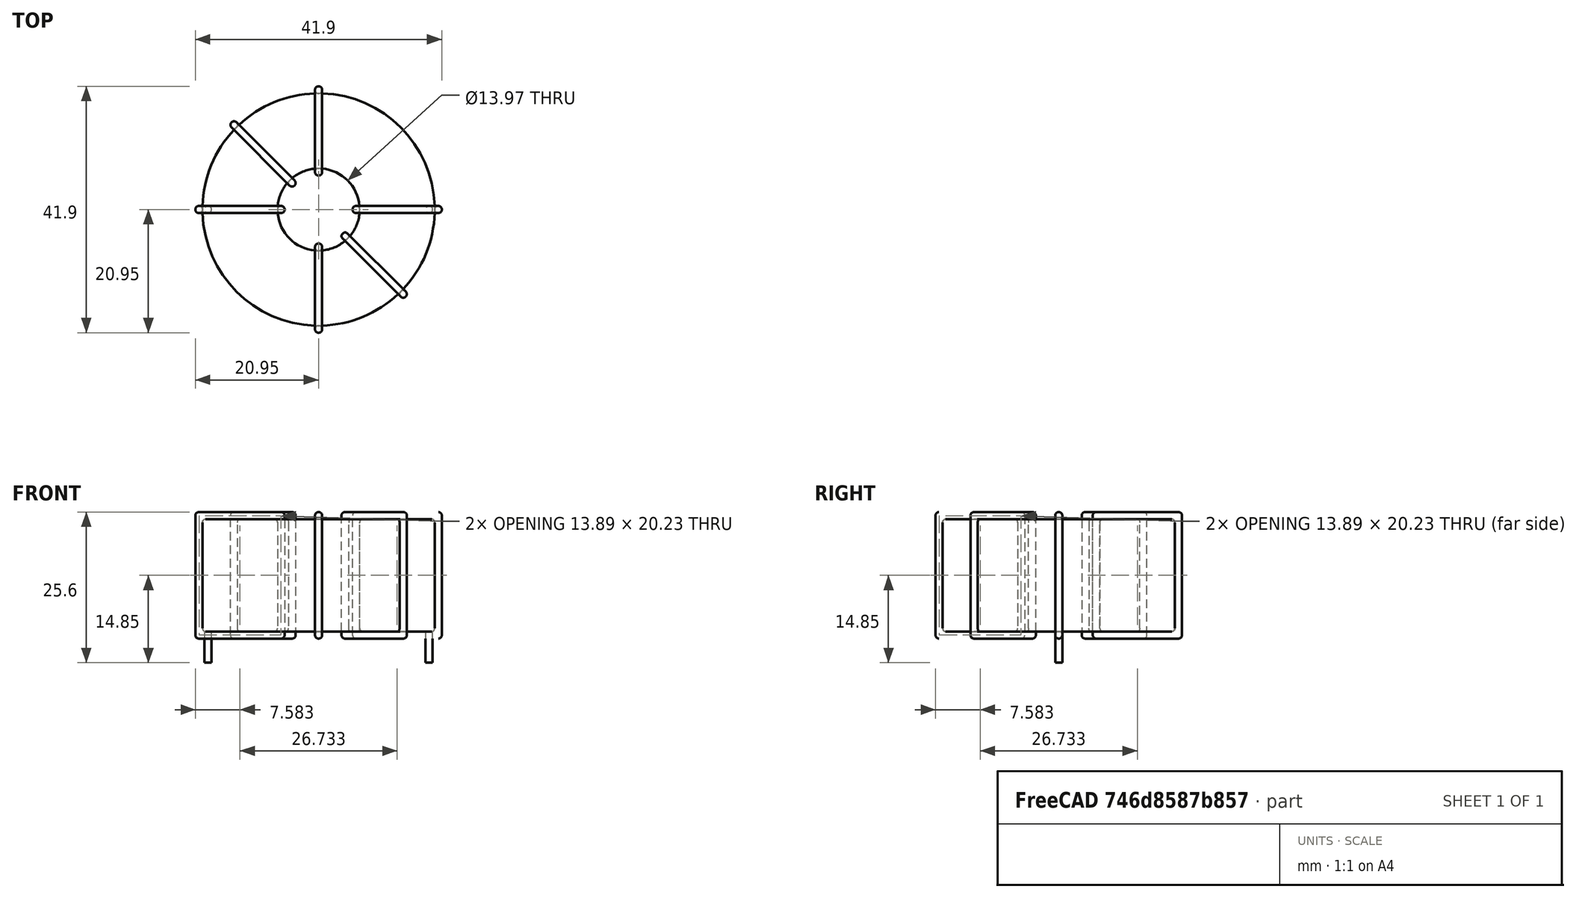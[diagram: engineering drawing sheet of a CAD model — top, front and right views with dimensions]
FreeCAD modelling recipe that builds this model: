
FCSTD DOCUMENT  (FreeCAD 0.16R6703 (Git))
Label: L_Toroid_Horizontal_D41.9mm_P37.60mm_Vishay_TJ7
License: All rights reserved
LicenseURL: http://en.wikipedia.org/wiki/All_rights_reserved
objects: Sketcher::SketchObject×6, PartDesign::Pad×6, PartDesign::Fillet×5, Spreadsheet::Sheet×1
note: 23 computed .brp shape members not serialized (recipe doc carries the construction recipe); baked Part::Feature solids carry a one-line shape summary decoded from their .brp

FEATURE [Spreadsheet::Sheet] Spreadsheet  label="dimensions"
  cells = A1=Wx; B1(Wx)=41.9; C1(WW)=13.96666666666667; D1=41.9; A2=Wy; B2(Wy)=41.9; D2=41.9; A3=RM; B3(RMx)=37.6; C3(RMy)=0; A4=d_wire; B4(d_wire)=1.2; A5=H; B5(H)=19.1; A6=offsetx; B6(offsetx)=2.149999999999999
FEATURE [Sketcher::SketchObject] Sketch
  Placement = pos=(0,0,1.7) rot=(0,0,1;0rad)
  expr: Placement.Base.z = 0.5 + Spreadsheet.d_wire
  expr: Constraints[0] = Spreadsheet.Wx / 2 - Spreadsheet.d_wire
  expr: Constraints[4] = Spreadsheet.WW / 2
  expr: Constraints[2] = Spreadsheet.RMy / 2
  expr: Constraints[1] = Spreadsheet.RMx / 2
  sketch-geometry (2):
    g0: Circle CenterX=18.8 CenterY=0 CenterZ=0 NormalX=0 NormalY=0 NormalZ=1 Radius=19.75
    g1: Circle CenterX=18.8 CenterY=0 CenterZ=0 NormalX=0 NormalY=0 NormalZ=1 Radius=6.98333
  constraints (5):
    c: Radius(g0) = 19.75
    c: DistanceX(g-1,g0) = 18.8
    c: DistanceY(g-1,g0) = 0
    c: Coincident(g1,g0)
    c: Radius(g1) = 6.98333
FEATURE [PartDesign::Pad] Pad
  Length = 19.1
  Length2 = 100
  Placement = pos=(0,0,1.7) rot=(0,0,1;0rad)
  Sketch = -> Sketch
  Type = 0
  expr: Length = Spreadsheet.H
FEATURE [Sketcher::SketchObject] Sketch001
  Placement = pos=(0,0,1.1) rot=(0,0,1;0rad)
  expr: Placement.Base.z = 0.5 + Spreadsheet.d_wire * 0.5
  expr: Constraints[4] = Spreadsheet.RMx
  expr: Constraints[2] = Spreadsheet.RMy
  expr: Constraints[1] = Spreadsheet.d_wire / 2
  sketch-geometry (2):
    g0: Circle CenterX=0 CenterY=0 CenterZ=0 NormalX=0 NormalY=0 NormalZ=1 Radius=0.6
    g1: Circle CenterX=37.6 CenterY=0 CenterZ=0 NormalX=0 NormalY=0 NormalZ=1 Radius=0.6
  constraints (5):
    c: Equal(g0,g1)
    c: Radius(g0) = 0.6
    c: DistanceY(g-1,g1) = 0
    c: Coincident(g0,g-1)
    c: DistanceX(g-1,g1) = 37.6
FEATURE [PartDesign::Pad] Pad001
  Length = 0.6
  Length2 = 4.7
  Placement = pos=(0,0,1.1) rot=(0,0,1;0rad)
  Reversed = true
  Sketch = -> Sketch001
  Type = 4
  expr: Length2 = 3.5 + Spreadsheet.d_wire
  expr: Length = Spreadsheet.d_wire / 2
FEATURE [PartDesign::Fillet] Fillet
  Base = -> Pad [Edge6,Edge3,Edge2]
  Placement = pos=(0,0,1.7) rot=(0,0,1;0rad)
  Radius = 0.5
FEATURE [Sketcher::SketchObject] Sketch003
  Placement = pos=(18.8,0,0) rot=(1,0,0;1.5708rad)
  expr: Placement.Base.x = Spreadsheet.RMx / 2
  expr: Constraints[49] = Spreadsheet.Wx - Spreadsheet.d_wire * 2
  expr: Constraints[44] = Spreadsheet.d_wire
  expr: Constraints[23] = Spreadsheet.H
  expr: Constraints[22] = Spreadsheet.Wx / 2 - Spreadsheet.d_wire
  expr: Placement.Base.y = Spreadsheet.RMy / 2
  expr: Constraints[21] = (Spreadsheet.Wx - Spreadsheet.WW) / 2 - Spreadsheet.d_wire
  expr: Constraints[19] = Spreadsheet.d_wire
  expr: Constraints[17] = Spreadsheet.d_wire
  expr: Constraints[18] = Spreadsheet.d_wire
  expr: Constraints[16] = Spreadsheet.d_wire
  sketch-geometry (16):
    g0: LineSegment StartX=-5.78333 StartY=0.5 StartZ=0 EndX=-20.95 EndY=0.5 EndZ=0
    g1: LineSegment StartX=-20.95 StartY=0.5 StartZ=0 EndX=-20.95 EndY=22 EndZ=0
    g2: LineSegment StartX=-20.95 StartY=22 StartZ=0 EndX=-5.78333 EndY=22 EndZ=0
    g3: LineSegment StartX=-5.78333 StartY=22 StartZ=0 EndX=-5.78333 EndY=0.5 EndZ=0
    g4: LineSegment StartX=-19.75 StartY=20.8 StartZ=0 EndX=-6.98333 EndY=20.8 EndZ=0
    g5: LineSegment StartX=-6.98333 StartY=20.8 StartZ=0 EndX=-6.98333 EndY=1.7 EndZ=0
    g6: LineSegment StartX=-6.98333 StartY=1.7 StartZ=0 EndX=-19.75 EndY=1.7 EndZ=0
    g7: LineSegment StartX=-19.75 StartY=1.7 StartZ=0 EndX=-19.75 EndY=20.8 EndZ=0
    g8: LineSegment StartX=5.78333 StartY=22 StartZ=0 EndX=20.95 EndY=22 EndZ=0
    g9: LineSegment StartX=20.95 StartY=22 StartZ=0 EndX=20.95 EndY=0.5 EndZ=0
    g10: LineSegment StartX=20.95 StartY=0.5 StartZ=0 EndX=5.78333 EndY=0.5 EndZ=0
    g11: LineSegment StartX=5.78333 StartY=0.5 StartZ=0 EndX=5.78333 EndY=22 EndZ=0
    g12: LineSegment StartX=6.98333 StartY=20.8 StartZ=0 EndX=19.75 EndY=20.8 EndZ=0
    g13: LineSegment StartX=19.75 StartY=20.8 StartZ=0 EndX=19.75 EndY=1.7 EndZ=0
    g14: LineSegment StartX=19.75 StartY=1.7 StartZ=0 EndX=6.98333 EndY=1.7 EndZ=0
    g15: LineSegment StartX=6.98333 StartY=1.7 StartZ=0 EndX=6.98333 EndY=20.8 EndZ=0
  constraints (50):
    c: Horizontal(g0)
    c: Coincident(g1,g0)
    c: Vertical(g1)
    c: Coincident(g2,g1)
    c: Horizontal(g2)
    c: Coincident(g3,g2)
    c: Coincident(g3,g0)
    c: Vertical(g3)
    c: Coincident(g4,g5)
    c: Coincident(g5,g6)
    c: Coincident(g6,g7)
    c: Coincident(g7,g4)
    c: Horizontal(g4)
    c: Horizontal(g6)
    c: Vertical(g5)
    c: Vertical(g7)
    c: DistanceX(g1,g4) = 1.2
    c: DistanceY(g4,g1) = 1.2
    c: DistanceX(g5,g0) = 1.2
    c: DistanceY(g0,g5) = 1.2
    c: DistanceY(g-1,g0) = 0.5
    c: DistanceX(g6,g6) = 12.7667
    c: DistanceX(g6,g-1) = 19.75
    c: DistanceY(g7,g7) = 19.1
    c: Coincident(g8,g9)
    c: Coincident(g9,g10)
    c: Coincident(g10,g11)
    c: Coincident(g11,g8)
    c: Horizontal(g8)
    c: Horizontal(g10)
    c: Vertical(g9)
    c: Vertical(g11)
    c: Coincident(g12,g13)
    c: Coincident(g13,g14)
    c: Coincident(g14,g15)
    c: Coincident(g15,g12)
    c: Horizontal(g12)
    c: Horizontal(g14)
    c: Vertical(g13)
    c: Vertical(g15)
    c: DistanceY(g8,g2) = 0
    c: DistanceY(g10,g0) = 0
    c: DistanceY(g14,g5) = 0
    c: DistanceY(g12,g4) = 0
    c: DistanceX(g8,g12) = 1.2
    c: Equal(g8,g2)
    c: Equal(g12,g4)
    c: Equal(g9,g1)
    c: Equal(g13,g7)
    c: DistanceX(g4,g12) = 39.5
FEATURE [PartDesign::Pad] Pad002
  Length = 1.2
  Length2 = 100
  Midplane = true
  Placement = pos=(18.8,0,0) rot=(1,0,0;1.5708rad)
  Sketch = -> Sketch003
  Type = 0
  expr: Length = Spreadsheet.d_wire
FEATURE [PartDesign::Fillet] Fillet001
  Base = -> Pad002 [Edge38,Edge41,Edge42,Edge43,Edge29,Edge32,Edge33,Edge34,Edge25,Edge35,Edge36,Edge13,Edge14,Edge15,Edge16,Edge17,Edge18,Edge19,Edge1,Edge2,Edge3,Edge4,Edge5,Edge6,Edge7,Edge37,Edge39,Edge40,Edge20,Edge23,Edge24,Edge21,Edge22,Edge8,Edge9,Edge10,Edge11,Edge12,Edge26,Edge27,+8 more]
  Placement = pos=(18.8,0,0) rot=(1,0,0;1.5708rad)
  Radius = 0.564
  expr: Radius = Spreadsheet.d_wire * 0.47
FEATURE [Sketcher::SketchObject] Sketch004
  Placement = pos=(18.8,0,0) rot=(0.862856,0.357407,0.357407;1.71777rad)
  expr: Placement.Base.x = Spreadsheet.RMx / 2
  expr: Constraints[49] = Spreadsheet.Wx - 2 * Spreadsheet.d_wire
  expr: Constraints[44] = Spreadsheet.d_wire
  expr: Constraints[23] = Spreadsheet.H
  expr: Constraints[22] = Spreadsheet.Wx / 2 - Spreadsheet.d_wire
  expr: Placement.Base.y = Spreadsheet.RMy / 2
  expr: Constraints[21] = (Spreadsheet.Wx - Spreadsheet.WW) / 2 - Spreadsheet.d_wire
  expr: Constraints[19] = Spreadsheet.d_wire
  expr: Constraints[17] = Spreadsheet.d_wire
  expr: Constraints[18] = Spreadsheet.d_wire
  expr: Constraints[16] = Spreadsheet.d_wire
  sketch-geometry (16):
    g0: LineSegment StartX=-5.78333 StartY=0.5 StartZ=0 EndX=-20.95 EndY=0.5 EndZ=0
    g1: LineSegment StartX=-20.95 StartY=0.5 StartZ=0 EndX=-20.95 EndY=22 EndZ=0
    g2: LineSegment StartX=-20.95 StartY=22 StartZ=0 EndX=-5.78333 EndY=22 EndZ=0
    g3: LineSegment StartX=-5.78333 StartY=22 StartZ=0 EndX=-5.78333 EndY=0.5 EndZ=0
    g4: LineSegment StartX=-19.75 StartY=20.8 StartZ=0 EndX=-6.98333 EndY=20.8 EndZ=0
    g5: LineSegment StartX=-6.98333 StartY=20.8 StartZ=0 EndX=-6.98333 EndY=1.7 EndZ=0
    g6: LineSegment StartX=-6.98333 StartY=1.7 StartZ=0 EndX=-19.75 EndY=1.7 EndZ=0
    g7: LineSegment StartX=-19.75 StartY=1.7 StartZ=0 EndX=-19.75 EndY=20.8 EndZ=0
    g8: LineSegment StartX=5.78333 StartY=22 StartZ=0 EndX=20.95 EndY=22 EndZ=0
    g9: LineSegment StartX=20.95 StartY=22 StartZ=0 EndX=20.95 EndY=0.5 EndZ=0
    g10: LineSegment StartX=20.95 StartY=0.5 StartZ=0 EndX=5.78333 EndY=0.5 EndZ=0
    g11: LineSegment StartX=5.78333 StartY=0.5 StartZ=0 EndX=5.78333 EndY=22 EndZ=0
    g12: LineSegment StartX=6.98333 StartY=20.8 StartZ=0 EndX=19.75 EndY=20.8 EndZ=0
    g13: LineSegment StartX=19.75 StartY=20.8 StartZ=0 EndX=19.75 EndY=1.7 EndZ=0
    g14: LineSegment StartX=19.75 StartY=1.7 StartZ=0 EndX=6.98333 EndY=1.7 EndZ=0
    g15: LineSegment StartX=6.98333 StartY=1.7 StartZ=0 EndX=6.98333 EndY=20.8 EndZ=0
  constraints (50):
    c: Horizontal(g0)
    c: Coincident(g1,g0)
    c: Vertical(g1)
    c: Coincident(g2,g1)
    c: Horizontal(g2)
    c: Coincident(g3,g2)
    c: Coincident(g3,g0)
    c: Vertical(g3)
    c: Coincident(g4,g5)
    c: Coincident(g5,g6)
    c: Coincident(g6,g7)
    c: Coincident(g7,g4)
    c: Horizontal(g4)
    c: Horizontal(g6)
    c: Vertical(g5)
    c: Vertical(g7)
    c: DistanceX(g1,g4) = 1.2
    c: DistanceY(g4,g1) = 1.2
    c: DistanceX(g5,g0) = 1.2
    c: DistanceY(g0,g5) = 1.2
    c: DistanceY(g-1,g0) = 0.5
    c: DistanceX(g6,g6) = 12.7667
    c: DistanceX(g6,g-1) = 19.75
    c: DistanceY(g7,g7) = 19.1
    c: Coincident(g8,g9)
    c: Coincident(g9,g10)
    c: Coincident(g10,g11)
    c: Coincident(g11,g8)
    c: Horizontal(g8)
    c: Horizontal(g10)
    c: Vertical(g9)
    c: Vertical(g11)
    c: Coincident(g12,g13)
    c: Coincident(g13,g14)
    c: Coincident(g14,g15)
    c: Coincident(g15,g12)
    c: Horizontal(g12)
    c: Horizontal(g14)
    c: Vertical(g13)
    c: Vertical(g15)
    c: DistanceY(g8,g2) = 0
    c: DistanceY(g10,g0) = 0
    c: DistanceY(g14,g5) = 0
    c: DistanceY(g12,g4) = 0
    c: DistanceX(g8,g12) = 1.2
    c: Equal(g8,g2)
    c: Equal(g12,g4)
    c: Equal(g9,g1)
    c: Equal(g13,g7)
    c: DistanceX(g4,g12) = 39.5
FEATURE [PartDesign::Pad] Pad003
  Length = 1.2
  Length2 = 100
  Midplane = true
  Placement = pos=(18.8,0,0) rot=(0.862856,0.357407,0.357407;1.71777rad)
  Sketch = -> Sketch004
  Type = 0
  expr: Length = Spreadsheet.d_wire
FEATURE [PartDesign::Fillet] Fillet002
  Base = -> Pad003 [Edge38,Edge41,Edge42,Edge43,Edge29,Edge32,Edge33,Edge34,Edge25,Edge35,Edge36,Edge13,Edge14,Edge15,Edge16,Edge17,Edge18,Edge19,Edge1,Edge2,Edge3,Edge4,Edge5,Edge6,Edge7,Edge37,Edge39,Edge40,Edge20,Edge23,Edge24,Edge21,Edge22,Edge8,Edge9,Edge10,Edge11,Edge12,Edge26,Edge27,+8 more]
  Placement = pos=(18.8,0,0) rot=(0.862856,0.357407,0.357407;1.71777rad)
  Radius = 0.564
  expr: Radius = Spreadsheet.d_wire * 0.47
FEATURE [Sketcher::SketchObject] Sketch005
  Placement = pos=(18.8,0,0) rot=(0.862856,-0.357407,-0.357407;1.71777rad)
  expr: Placement.Base.x = Spreadsheet.RMx / 2
  expr: Constraints[49] = Spreadsheet.Wx - 2 * Spreadsheet.d_wire
  expr: Constraints[44] = Spreadsheet.d_wire
  expr: Constraints[23] = Spreadsheet.H
  expr: Constraints[22] = Spreadsheet.Wx / 2 - Spreadsheet.d_wire
  expr: Placement.Base.y = Spreadsheet.RMy / 2
  expr: Constraints[21] = (Spreadsheet.Wx - Spreadsheet.WW) / 2 - Spreadsheet.d_wire
  expr: Constraints[19] = Spreadsheet.d_wire
  expr: Constraints[17] = Spreadsheet.d_wire
  expr: Constraints[18] = Spreadsheet.d_wire
  expr: Constraints[16] = Spreadsheet.d_wire
  sketch-geometry (16):
    g0: LineSegment StartX=-5.78333 StartY=0.5 StartZ=0 EndX=-20.95 EndY=0.5 EndZ=0
    g1: LineSegment StartX=-20.95 StartY=0.5 StartZ=0 EndX=-20.95 EndY=22 EndZ=0
    g2: LineSegment StartX=-20.95 StartY=22 StartZ=0 EndX=-5.78333 EndY=22 EndZ=0
    g3: LineSegment StartX=-5.78333 StartY=22 StartZ=0 EndX=-5.78333 EndY=0.5 EndZ=0
    g4: LineSegment StartX=-19.75 StartY=20.8 StartZ=0 EndX=-6.98333 EndY=20.8 EndZ=0
    g5: LineSegment StartX=-6.98333 StartY=20.8 StartZ=0 EndX=-6.98333 EndY=1.7 EndZ=0
    g6: LineSegment StartX=-6.98333 StartY=1.7 StartZ=0 EndX=-19.75 EndY=1.7 EndZ=0
    g7: LineSegment StartX=-19.75 StartY=1.7 StartZ=0 EndX=-19.75 EndY=20.8 EndZ=0
    g8: LineSegment StartX=5.78333 StartY=22 StartZ=0 EndX=20.95 EndY=22 EndZ=0
    g9: LineSegment StartX=20.95 StartY=22 StartZ=0 EndX=20.95 EndY=0.5 EndZ=0
    g10: LineSegment StartX=20.95 StartY=0.5 StartZ=0 EndX=5.78333 EndY=0.5 EndZ=0
    g11: LineSegment StartX=5.78333 StartY=0.5 StartZ=0 EndX=5.78333 EndY=22 EndZ=0
    g12: LineSegment StartX=6.98333 StartY=20.8 StartZ=0 EndX=19.75 EndY=20.8 EndZ=0
    g13: LineSegment StartX=19.75 StartY=20.8 StartZ=0 EndX=19.75 EndY=1.7 EndZ=0
    g14: LineSegment StartX=19.75 StartY=1.7 StartZ=0 EndX=6.98333 EndY=1.7 EndZ=0
    g15: LineSegment StartX=6.98333 StartY=1.7 StartZ=0 EndX=6.98333 EndY=20.8 EndZ=0
  constraints (50):
    c: Horizontal(g0)
    c: Coincident(g1,g0)
    c: Vertical(g1)
    c: Coincident(g2,g1)
    c: Horizontal(g2)
    c: Coincident(g3,g2)
    c: Coincident(g3,g0)
    c: Vertical(g3)
    c: Coincident(g4,g5)
    c: Coincident(g5,g6)
    c: Coincident(g6,g7)
    c: Coincident(g7,g4)
    c: Horizontal(g4)
    c: Horizontal(g6)
    c: Vertical(g5)
    c: Vertical(g7)
    c: DistanceX(g1,g4) = 1.2
    c: DistanceY(g4,g1) = 1.2
    c: DistanceX(g5,g0) = 1.2
    c: DistanceY(g0,g5) = 1.2
    c: DistanceY(g-1,g0) = 0.5
    c: DistanceX(g6,g6) = 12.7667
    c: DistanceX(g6,g-1) = 19.75
    c: DistanceY(g7,g7) = 19.1
    c: Coincident(g8,g9)
    c: Coincident(g9,g10)
    c: Coincident(g10,g11)
    c: Coincident(g11,g8)
    c: Horizontal(g8)
    c: Horizontal(g10)
    c: Vertical(g9)
    c: Vertical(g11)
    c: Coincident(g12,g13)
    c: Coincident(g13,g14)
    c: Coincident(g14,g15)
    c: Coincident(g15,g12)
    c: Horizontal(g12)
    c: Horizontal(g14)
    c: Vertical(g13)
    c: Vertical(g15)
    c: DistanceY(g8,g2) = 0
    c: DistanceY(g10,g0) = 0
    c: DistanceY(g14,g5) = 0
    c: DistanceY(g12,g4) = 0
    c: DistanceX(g8,g12) = 1.2
    c: Equal(g8,g2)
    c: Equal(g12,g4)
    c: Equal(g9,g1)
    c: Equal(g13,g7)
    c: DistanceX(g4,g12) = 39.5
FEATURE [PartDesign::Pad] Pad004
  Length = 1.2
  Length2 = 100
  Midplane = true
  Placement = pos=(18.8,0,0) rot=(0.862856,-0.357407,-0.357407;1.71777rad)
  Sketch = -> Sketch005
  Type = 0
  expr: Length = Spreadsheet.d_wire
FEATURE [PartDesign::Fillet] Fillet003
  Base = -> Pad004 [Edge38,Edge41,Edge42,Edge43,Edge29,Edge32,Edge33,Edge34,Edge25,Edge35,Edge36,Edge13,Edge14,Edge15,Edge16,Edge17,Edge18,Edge19,Edge1,Edge2,Edge3,Edge4,Edge5,Edge6,Edge7,Edge37,Edge39,Edge40,Edge20,Edge23,Edge24,Edge21,Edge22,Edge8,Edge9,Edge10,Edge11,Edge12,Edge26,Edge27,+8 more]
  Placement = pos=(18.8,0,0) rot=(0.862856,-0.357407,-0.357407;1.71777rad)
  Radius = 0.564
  expr: Radius = Spreadsheet.d_wire * 0.47
FEATURE [Sketcher::SketchObject] Sketch006
  Placement = pos=(18.8,0,0) rot=(0.57735,0.57735,0.57735;2.0944rad)
  expr: Placement.Base.x = Spreadsheet.RMx / 2
  expr: Constraints[49] = Spreadsheet.Wx - Spreadsheet.d_wire * 2
  expr: Constraints[44] = Spreadsheet.d_wire
  expr: Constraints[23] = Spreadsheet.H
  expr: Constraints[22] = Spreadsheet.Wx / 2 - Spreadsheet.d_wire
  expr: Placement.Base.y = Spreadsheet.RMy / 2
  expr: Constraints[21] = (Spreadsheet.Wx - Spreadsheet.WW) / 2 - Spreadsheet.d_wire
  expr: Constraints[19] = Spreadsheet.d_wire
  expr: Constraints[17] = Spreadsheet.d_wire
  expr: Constraints[18] = Spreadsheet.d_wire
  expr: Constraints[16] = Spreadsheet.d_wire
  sketch-geometry (16):
    g0: LineSegment StartX=-5.78333 StartY=0.5 StartZ=0 EndX=-20.95 EndY=0.5 EndZ=0
    g1: LineSegment StartX=-20.95 StartY=0.5 StartZ=0 EndX=-20.95 EndY=22 EndZ=0
    g2: LineSegment StartX=-20.95 StartY=22 StartZ=0 EndX=-5.78333 EndY=22 EndZ=0
    g3: LineSegment StartX=-5.78333 StartY=22 StartZ=0 EndX=-5.78333 EndY=0.5 EndZ=0
    g4: LineSegment StartX=-19.75 StartY=20.8 StartZ=0 EndX=-6.98333 EndY=20.8 EndZ=0
    g5: LineSegment StartX=-6.98333 StartY=20.8 StartZ=0 EndX=-6.98333 EndY=1.7 EndZ=0
    g6: LineSegment StartX=-6.98333 StartY=1.7 StartZ=0 EndX=-19.75 EndY=1.7 EndZ=0
    g7: LineSegment StartX=-19.75 StartY=1.7 StartZ=0 EndX=-19.75 EndY=20.8 EndZ=0
    g8: LineSegment StartX=5.78333 StartY=22 StartZ=0 EndX=20.95 EndY=22 EndZ=0
    g9: LineSegment StartX=20.95 StartY=22 StartZ=0 EndX=20.95 EndY=0.5 EndZ=0
    g10: LineSegment StartX=20.95 StartY=0.5 StartZ=0 EndX=5.78333 EndY=0.5 EndZ=0
    g11: LineSegment StartX=5.78333 StartY=0.5 StartZ=0 EndX=5.78333 EndY=22 EndZ=0
    g12: LineSegment StartX=6.98333 StartY=20.8 StartZ=0 EndX=19.75 EndY=20.8 EndZ=0
    g13: LineSegment StartX=19.75 StartY=20.8 StartZ=0 EndX=19.75 EndY=1.7 EndZ=0
    g14: LineSegment StartX=19.75 StartY=1.7 StartZ=0 EndX=6.98333 EndY=1.7 EndZ=0
    g15: LineSegment StartX=6.98333 StartY=1.7 StartZ=0 EndX=6.98333 EndY=20.8 EndZ=0
  constraints (50):
    c: Horizontal(g0)
    c: Coincident(g1,g0)
    c: Vertical(g1)
    c: Coincident(g2,g1)
    c: Horizontal(g2)
    c: Coincident(g3,g2)
    c: Coincident(g3,g0)
    c: Vertical(g3)
    c: Coincident(g4,g5)
    c: Coincident(g5,g6)
    c: Coincident(g6,g7)
    c: Coincident(g7,g4)
    c: Horizontal(g4)
    c: Horizontal(g6)
    c: Vertical(g5)
    c: Vertical(g7)
    c: DistanceX(g1,g4) = 1.2
    c: DistanceY(g4,g1) = 1.2
    c: DistanceX(g5,g0) = 1.2
    c: DistanceY(g0,g5) = 1.2
    c: DistanceY(g-1,g0) = 0.5
    c: DistanceX(g6,g6) = 12.7667
    c: DistanceX(g6,g-1) = 19.75
    c: DistanceY(g7,g7) = 19.1
    c: Coincident(g8,g9)
    c: Coincident(g9,g10)
    c: Coincident(g10,g11)
    c: Coincident(g11,g8)
    c: Horizontal(g8)
    c: Horizontal(g10)
    c: Vertical(g9)
    c: Vertical(g11)
    c: Coincident(g12,g13)
    c: Coincident(g13,g14)
    c: Coincident(g14,g15)
    c: Coincident(g15,g12)
    c: Horizontal(g12)
    c: Horizontal(g14)
    c: Vertical(g13)
    c: Vertical(g15)
    c: DistanceY(g8,g2) = 0
    c: DistanceY(g10,g0) = 0
    c: DistanceY(g14,g5) = 0
    c: DistanceY(g12,g4) = 0
    c: DistanceX(g8,g12) = 1.2
    c: Equal(g8,g2)
    c: Equal(g12,g4)
    c: Equal(g9,g1)
    c: Equal(g13,g7)
    c: DistanceX(g4,g12) = 39.5
FEATURE [PartDesign::Pad] Pad005
  Length = 1.2
  Length2 = 100
  Midplane = true
  Placement = pos=(18.8,0,0) rot=(0.57735,0.57735,0.57735;2.0944rad)
  Sketch = -> Sketch006
  Type = 0
  expr: Length = Spreadsheet.d_wire
FEATURE [PartDesign::Fillet] Fillet004
  Base = -> Pad005 [Edge38,Edge41,Edge42,Edge43,Edge29,Edge32,Edge33,Edge34,Edge25,Edge35,Edge36,Edge13,Edge14,Edge15,Edge16,Edge17,Edge18,Edge19,Edge1,Edge2,Edge3,Edge4,Edge5,Edge6,Edge7,Edge37,Edge39,Edge40,Edge20,Edge23,Edge24,Edge21,Edge22,Edge8,Edge9,Edge10,Edge11,Edge12,Edge26,Edge27,+8 more]
  Placement = pos=(18.8,0,0) rot=(0.57735,0.57735,0.57735;2.0944rad)
  Radius = 0.564
  expr: Radius = Spreadsheet.d_wire * 0.47
